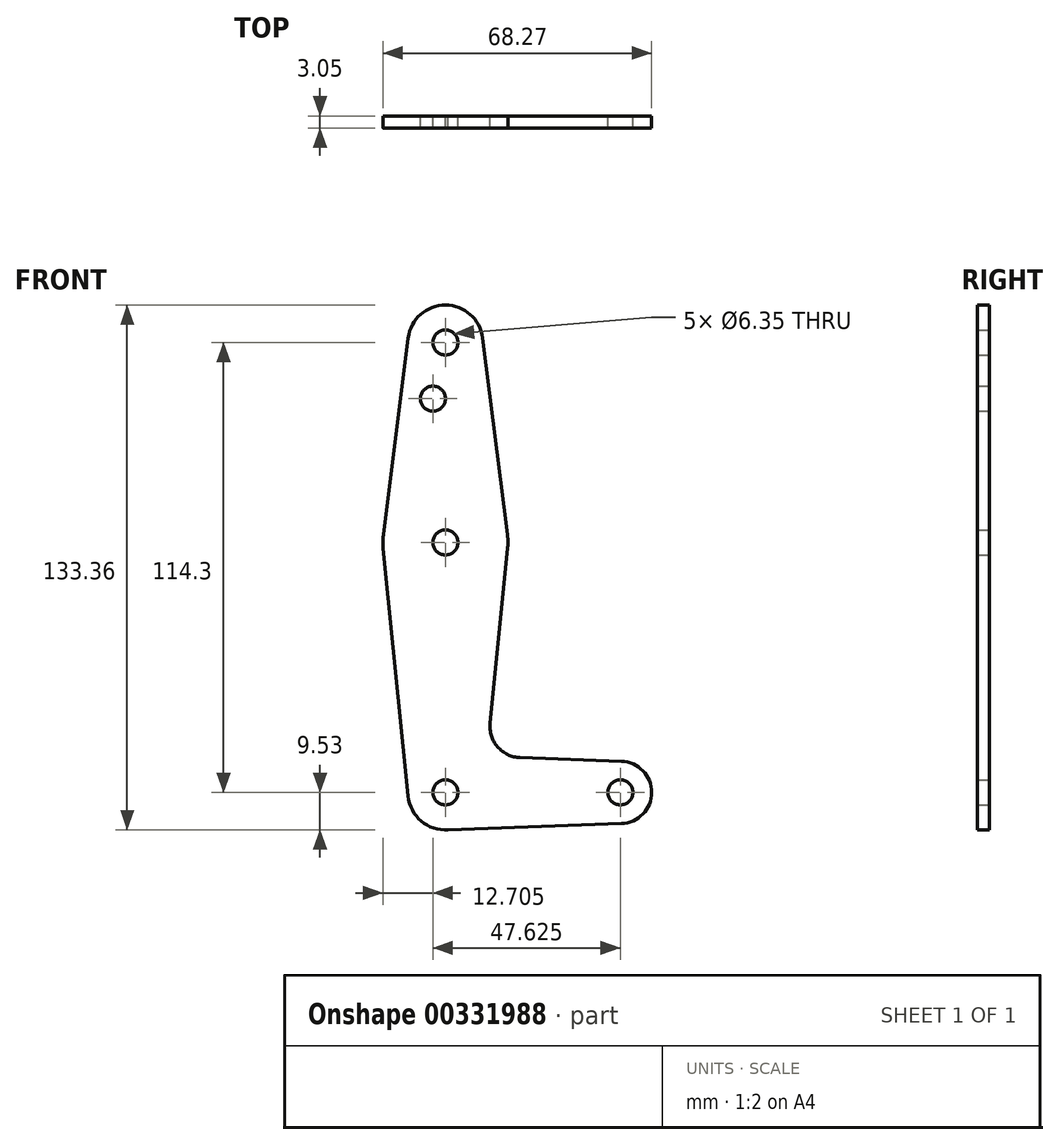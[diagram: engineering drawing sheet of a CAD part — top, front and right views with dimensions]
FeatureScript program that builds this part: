
annotation { "Feature Type Name" : "Feature", "Feature Type Description" : "" }
export const myFeature = defineFeature(function(context is Context, id is Id, definition is map)
    precondition{}
    {
        {
            var Q0;
            Q0=qCreatedBy(makeId("Front.planeOp"),FACE);
            var sketch = newSketch(context, id + "F0", { "sketchPlane" : qUnion([Q0])});
            skLineSegment(sketch, "E0", {"start": v(0, 0) * mm, "end": v(0, 114.3) * mm, "construction": true});
            skLineSegment(sketch, "E1", {"start": v(0, 0) * mm, "end": v(44.45, 0) * mm, "construction": true});
            skCircle(sketch, "E2", {"center": v(0, 114.3) * mm, "radius": 9.53 * mm});
            skCircle(sketch, "E3", {"center": v(0, 0) * mm, "radius": 9.53 * mm});
            skCircle(sketch, "E4", {"center": v(0, 63.5) * mm, "radius": 15.88 * mm});
            skCircle(sketch, "E5", {"center": v(44.45, 0) * mm, "radius": 7.94 * mm});
            skLineSegment(sketch, "E6", {"start": v(-9.45, 115.5) * mm, "end": v(-15.75, 65.48) * mm});
            skLineSegment(sketch, "E7", {"start": v(15.75, 65.48) * mm, "end": v(9.45, 115.5) * mm});
            skLineSegment(sketch, "E8", {"start": v(0, -9.53) * mm, "end": v(44.73, -7.93) * mm});
            skLineSegment(sketch, "E9", {"start": v(-15.8, 61.91) * mm, "end": v(-9.48, -0.95) * mm});
            skCircle(sketch, "E10", {"center": v(0, 114.3) * mm, "radius": 3.18 * mm});
            skCircle(sketch, "E11", {"center": v(0, 63.5) * mm, "radius": 3.18 * mm});
            skCircle(sketch, "E12", {"center": v(0, 0) * mm, "radius": 3.18 * mm});
            skCircle(sketch, "E13", {"center": v(44.45, 0) * mm, "radius": 3.18 * mm});
            skCircle(sketch, "E14", {"center": v(-3.18, 100.03) * mm, "radius": 3.18 * mm});
            skPoint(sketch, "E15.newPointA", {"position": v(9.48, -0.95) * mm});
            skLineSegment(sketch, "E16", {"start": v(11.34, 17.59) * mm, "end": v(15.8, 61.91) * mm});
            skLineSegment(sketch, "E17", {"start": v(18.97, 8.85) * mm, "end": v(44.73, 7.93) * mm});
            skArc(sketch, "E18.filletArc", {"start": v(11.34, 17.59) * mm, "mid": v(13.26, 11.57) * mm, "end": v(18.97, 8.85) * mm});
            skSolve(sketch);
        }
        {
            var Q0;
            Q0 = qSketchRegion(id + "F0", true);
            extrude(context, id + "F1", {"entities" : qUnion([Q0]), "depth" : 3.05 * mm});
        }
    });
